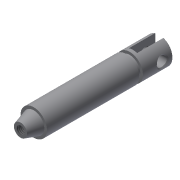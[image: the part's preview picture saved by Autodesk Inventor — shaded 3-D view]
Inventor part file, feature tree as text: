
AUTODESK INVENTOR PART (.ipt)
format: ipt  version: 2018.1 (Build 221171000, 171)  size: 158,720 bytes
history: native  units: mm
features: other x2, hole x2, chamfer x2, revolve x1, extrude x1, sketch x1
ambient origin geometry x8: Origin, YZ Plane, XZ Plane, XY Plane, X Axis, Y Axis, Z Axis, Center Point
bodies: Body1 (feature_tree)
feature tree (9):
  other  "kern"
  other  "Твердое тело1"
  revolve  "Вращение1"
  hole  "Отверстие1"  [1 undecoded]
  chamfer  "Фаска1"  Distance=8.0mm
  extrude  "Выдавливание1"  Depth=0.5mm
  hole  "Отверстие2"  [1 undecoded]
  chamfer  "Фаска2"  Angle=90.0deg  [1 undecoded]
  sketch  "Эскиз2"
note: 3 required parameter values undecoded (feature->parameter linkage not recoverable at this tier; creation-order binding heuristic only, values carry confidence <= 0.55)
